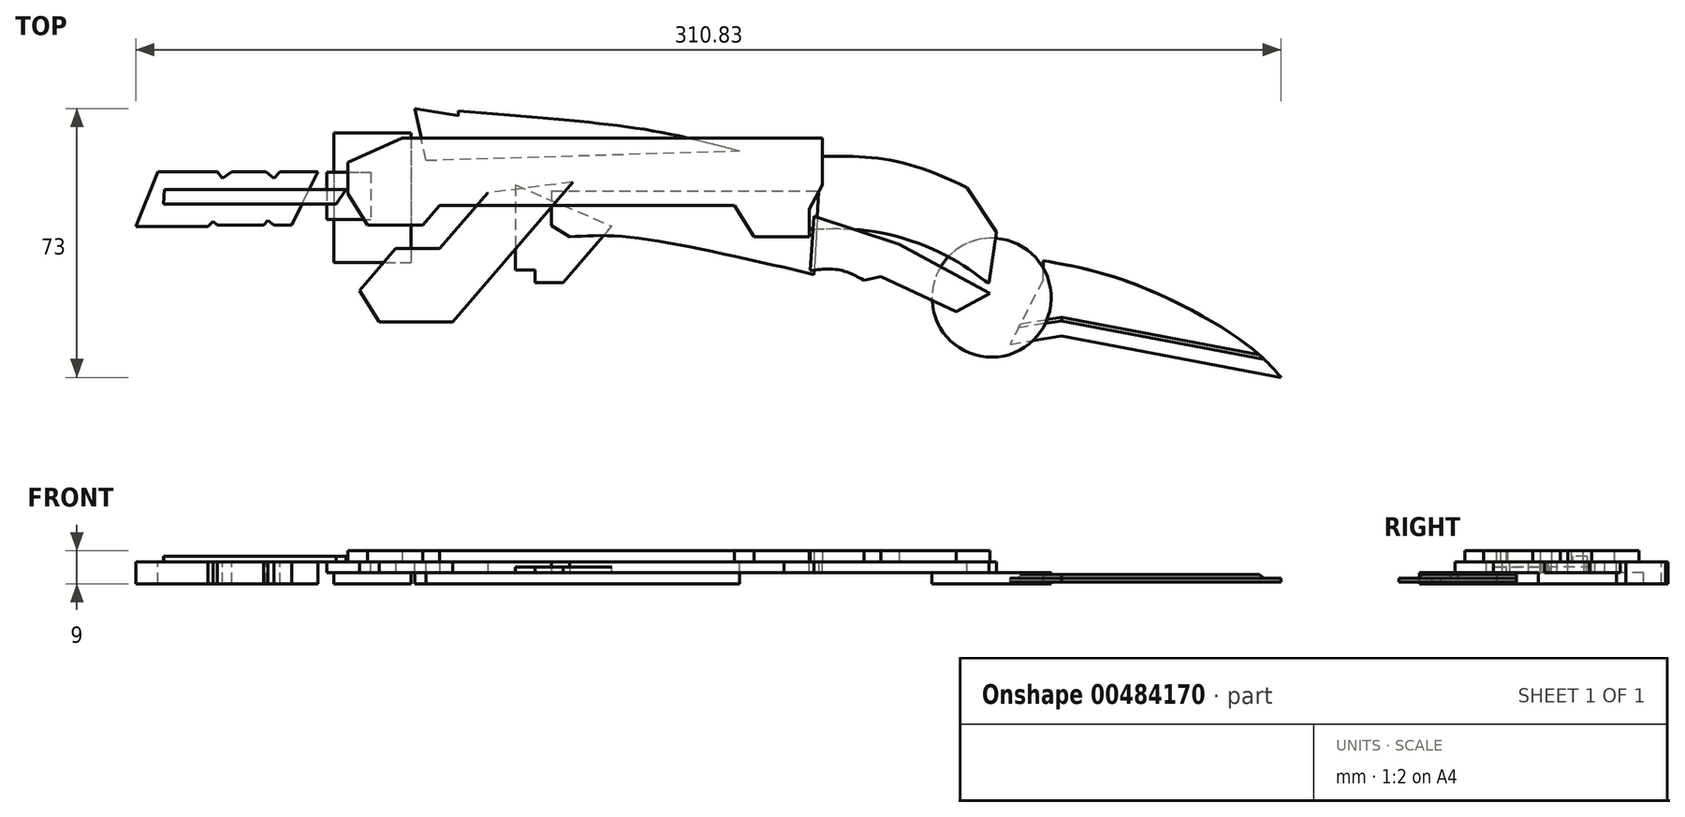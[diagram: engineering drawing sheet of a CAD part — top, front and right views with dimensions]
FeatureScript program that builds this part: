
annotation { "Feature Type Name" : "Feature", "Feature Type Description" : "" }
export const myFeature = defineFeature(function(context is Context, id is Id, definition is map)
    precondition{}
    {
        {
            var Q0;
            Q0=qCreatedBy(makeId("Top.planeOp"),FACE);
            var sketch = newSketch(context, id + "F0", { "sketchPlane" : qUnion([Q0])});
            skLineSegment(sketch, "E0", {"start": v(-55.32, 8.46) * mm, "end": v(-50, 0) * mm});
            skLineSegment(sketch, "E1", {"start": v(-50, 0) * mm, "end": v(-30, 0) * mm});
            skLineSegment(sketch, "E2", {"start": v(-30, 0) * mm, "end": v(2.6, 37.91) * mm});
            skLineSegment(sketch, "E3", {"start": v(-55.32, 8.46) * mm, "end": v(-45.54, 19.83) * mm});
            skLineSegment(sketch, "E4", {"start": v(-45.54, 19.83) * mm, "end": v(-33.54, 19.83) * mm});
            skLineSegment(sketch, "E5", {"start": v(-33.54, 19.83) * mm, "end": v(-20.5, 35) * mm});
            skLineSegment(sketch, "E6", {"start": v(2.6, 37.91) * mm, "end": v(-20.5, 35) * mm});
            skSolve(sketch);
        }
        {
            var Q0;
            Q0=makeQuery(id+"F0.imprint","IMPRINT",FACE,{"disambiguationData":[TD([[makeQuery(id+"F0.imprint","IMPRINT",EDGE,{"derivedFrom":sQuery(id+"F0.wireOp",EDGE,"E0")}),1.0]])]});
            extrude(context, id + "F1", {"entities" : qUnion([Q0]), "depth" : 3 * mm});
        }
        {
            var Q0;
            Q0=makeQuery(id+"F1.opExtrude","CAP_FACE",FACE,{"disambiguationData":[OSD([sQuery(id+"F0.wireOp",EDGE,"E0"),sQuery(id+"F0.wireOp",EDGE,"E1"),sQuery(id+"F0.wireOp",EDGE,"E2"),sQuery(id+"F0.wireOp",EDGE,"E3"),sQuery(id+"F0.wireOp",EDGE,"E4"),sQuery(id+"F0.wireOp",EDGE,"E5"),sQuery(id+"F0.wireOp",EDGE,"gxwEivb7-eXaO-3uHs-wTHl-g3tFR2Pt1wvS")])],"isStart":false});
            var sketch = newSketch(context, id + "F2", { "sketchPlane" : qUnion([Q0])});
            skLineSegment(sketch, "E7", {"start": v(-58.44, 34.7) * mm, "end": v(-53.1, 26.23) * mm});
            skLineSegment(sketch, "E8", {"start": v(-53.1, 26.23) * mm, "end": v(-38.1, 26.23) * mm});
            skLineSegment(sketch, "E9", {"start": v(-38.1, 26.23) * mm, "end": v(-33.54, 31.54) * mm});
            skLineSegment(sketch, "E10", {"start": v(-33.54, 31.54) * mm, "end": v(46.46, 31.54) * mm});
            skLineSegment(sketch, "E11", {"start": v(46.46, 31.54) * mm, "end": v(51.8, 23.08) * mm});
            skLineSegment(sketch, "E12", {"start": v(51.8, 23.08) * mm, "end": v(66.8, 23.08) * mm});
            skLineSegment(sketch, "E13", {"start": v(66.8, 23.08) * mm, "end": v(66.8, 30.58) * mm});
            skLineSegment(sketch, "E14", {"start": v(66.8, 30.58) * mm, "end": v(70.28, 37.11) * mm});
            skLineSegment(sketch, "E15", {"start": v(70.28, 37.11) * mm, "end": v(70.28, 49.91) * mm});
            skLineSegment(sketch, "E16", {"start": v(-58.44, 34.7) * mm, "end": v(-58.44, 43.2) * mm});
            skLineSegment(sketch, "E17", {"start": v(70.28, 49.91) * mm, "end": v(-43.72, 49.91) * mm});
            skLineSegment(sketch, "E18", {"start": v(-43.72, 49.91) * mm, "end": v(-58.44, 43.2) * mm});
            skSolve(sketch);
        }
        {
            var Q0;
            Q0=makeQuery(id+"F1.opExtrude","CAP_FACE",FACE,{"disambiguationData":[OSD([sQuery(id+"F0.wireOp",EDGE,"E0"),sQuery(id+"F0.wireOp",EDGE,"E1"),sQuery(id+"F0.wireOp",EDGE,"E2"),sQuery(id+"F0.wireOp",EDGE,"E3"),sQuery(id+"F0.wireOp",EDGE,"E4"),sQuery(id+"F0.wireOp",EDGE,"E5"),sQuery(id+"F0.wireOp",EDGE,"E6")])],"isStart":false});
            var sketch = newSketch(context, id + "F3", { "sketchPlane" : qUnion([Q0])});
            skLineSegment(sketch, "E19", {"start": v(-20.5, 35) * mm, "end": v(2.6, 37.91) * mm});
            skLineSegment(sketch, "E20", {"start": v(2.6, 37.91) * mm, "end": v(-2.86, 31.55) * mm});
            skLineSegment(sketch, "E21", {"start": v(-2.86, 31.55) * mm, "end": v(-23.48, 31.54) * mm});
            skLineSegment(sketch, "E22", {"start": v(-23.48, 31.54) * mm, "end": v(-20.5, 35) * mm});
            skSolve(sketch);
        }
        {
            var Q0;
            Q0 = qSketchRegion(id + "F3", true);
            extrude(context, id + "F4", {"entities" : qUnion([Q0]), "depth" : 3 * mm});
        }
        {
            var Q0;
            Q0 = qSketchRegion(id + "F2", true);
            extrude(context, id + "F5", {"entities" : qUnion([Q0]), "depth" : 3 * mm});
        }
        {
            var Q0;
            Q0=makeQuery(id+"F4.opExtrude","SWEPT_BODY",BODY,{"disambiguationData":[OSD([sQuery(id+"F3.wireOp",EDGE,"E19"),sQuery(id+"F3.wireOp",EDGE,"E20"),sQuery(id+"F3.wireOp",EDGE,"E21"),sQuery(id+"F3.wireOp",EDGE,"E22")])]});
            var Q1;
            Q1=makeQuery(id+"F5.opExtrude","SWEPT_BODY",BODY,{"disambiguationData":[OSD([sQuery(id+"F2.wireOp",EDGE,"E7"),sQuery(id+"F2.wireOp",EDGE,"E8"),sQuery(id+"F2.wireOp",EDGE,"E9"),sQuery(id+"F2.wireOp",EDGE,"E10"),sQuery(id+"F2.wireOp",EDGE,"E11"),sQuery(id+"F2.wireOp",EDGE,"E12"),sQuery(id+"F2.wireOp",EDGE,"E13"),sQuery(id+"F2.wireOp",EDGE,"E14"),sQuery(id+"F2.wireOp",EDGE,"E15"),sQuery(id+"F2.wireOp",EDGE,"E16"),sQuery(id+"F2.wireOp",EDGE,"E17"),sQuery(id+"F2.wireOp",EDGE,"E18")])]});
            booleanBodies(context, id + "F6", {"operationType" : BooleanOperationType.UNION, "tools" : qUnion([Q0, Q1])});
        }
        {
            var Q0;
            Q0=makeQuery(id+"F6.opBoolean","MERGE",FACE,{"derivedFrom":[makeQuery(id+"F4.opExtrude","CAP_FACE",FACE,{"disambiguationData":[OSD([sQuery(id+"F3.wireOp",EDGE,"E19"),sQuery(id+"F3.wireOp",EDGE,"E20"),sQuery(id+"F3.wireOp",EDGE,"E21"),sQuery(id+"F3.wireOp",EDGE,"E22")])],"isStart":true}),makeQuery(id+"F5.opExtrude","CAP_FACE",FACE,{"disambiguationData":[OSD([sQuery(id+"F2.wireOp",EDGE,"E7"),sQuery(id+"F2.wireOp",EDGE,"E8"),sQuery(id+"F2.wireOp",EDGE,"E9"),sQuery(id+"F2.wireOp",EDGE,"E10"),sQuery(id+"F2.wireOp",EDGE,"E11"),sQuery(id+"F2.wireOp",EDGE,"E12"),sQuery(id+"F2.wireOp",EDGE,"E13"),sQuery(id+"F2.wireOp",EDGE,"E14"),sQuery(id+"F2.wireOp",EDGE,"E15"),sQuery(id+"F2.wireOp",EDGE,"E16"),sQuery(id+"F2.wireOp",EDGE,"E17"),sQuery(id+"F2.wireOp",EDGE,"E18")])],"isStart":true})]});
            var sketch = newSketch(context, id + "F7", { "sketchPlane" : qUnion([Q0])});
            skFitSpline(sketch, "E23", {"points": [v(67.93, -44.79) * mm, v(91.44, -43.3) * mm, v(118.68, -31.91) * mm], "startDerivative": vector(49.42, -1.17) * mm, "endDerivative": vector(52.04, 26.4) * mm});
            skFitSpline(sketch, "E24", {"points": [v(62.89, -24.82) * mm, v(84.72, -24.45) * mm, v(107.67, -15.86) * mm, v(115.51, -10.45) * mm, v(115.89, -10.45) * mm], "startDerivative": vector(60.83, -3.9) * mm, "endDerivative": vector(6.34, -2.01) * mm});
            skLineSegment(sketch, "E25", {"start": v(67.93, -44.79) * mm, "end": v(62.89, -24.82) * mm});
            skLineSegment(sketch, "E26", {"start": v(117.56, -24.27) * mm, "end": v(115.51, -10.45) * mm});
            skLineSegment(sketch, "E27", {"start": v(109.52, -36.56) * mm, "end": v(117.56, -24.27) * mm});
            skSolve(sketch);
        }
        {
            var Q0;
            {var subQ0=sQuery(id+"F7.wireOp",EDGE,"E26");Q0=makeQuery(id+"F7.imprint","IMPRINT",FACE,{"disambiguationData":[TD([[makeQuery(id+"F7.imprint","IMPRINT",EDGE,{"derivedFrom":subQ0}),1.0]])]});}
            extrude(context, id + "F8", {"entities" : qUnion([Q0]), "depth" : 3 * mm});
        }
        {
            var Q0;
            Q0=makeQuery(id+"F8.opExtrude","CAP_FACE",FACE,{"disambiguationData":[OSD([sQuery(id+"F2.wireOp",EDGE,"E13"),sQuery(id+"F2.wireOp",EDGE,"E14"),sQuery(id+"F2.wireOp",EDGE,"E15"),sQuery(id+"F7.wireOp",EDGE,"E23"),sQuery(id+"F7.wireOp",EDGE,"E24"),sQuery(id+"F7.wireOp",EDGE,"E26"),sQuery(id+"F7.wireOp",EDGE,"E27")])],"isStart":false});
            var sketch = newSketch(context, id + "F9", { "sketchPlane" : qUnion([Q0])});
            skCircle(sketch, "E28", {"center": v(116.26, -6.53) * mm, "radius": 16.16 * mm});
            skSolve(sketch);
        }
        {
            var Q0;
            Q0 = qSketchRegion(id + "F9", true);
            extrude(context, id + "F10", {"entities" : qUnion([Q0]), "depth" : 3 * mm});
        }
        {
            var Q0;
            Q0=qCreatedBy(makeId("Top.planeOp"),FACE);
            cPlane(context, id + "F11", {"entities" : qUnion([Q0]), "cplaneType" : CPlaneType.OFFSET, "offset" : 1.5 * mm, "oppositeDirection" : true, "width" : 150 * mm, "height" : 150 * mm});
        }
        {
            var Q0;
            Q0=qCreatedBy(id+"F11.planeOp",FACE);
            var sketch = newSketch(context, id + "F12", { "sketchPlane" : qUnion([Q0])});
            skLineSegment(sketch, "E29", {"start": v(130.23, 11.38) * mm, "end": v(130.23, 16.6) * mm});
            skFitSpline(sketch, "E30", {"points": [v(130.23, 16.6) * mm, v(153.93, 10.64) * mm, v(184.83, -5.65) * mm, v(194.86, -15.15) * mm], "startDerivative": vector(65.46, -11.77) * mm, "endDerivative": vector(31.18, -35.34) * mm});
            skLineSegment(sketch, "E31", {"start": v(121.23, -6.18) * mm, "end": v(135.22, -3.8) * mm});
            skLineSegment(sketch, "E32", {"start": v(135.22, -3.8) * mm, "end": v(194.86, -15.15) * mm});
            skLineSegment(sketch, "E33", {"start": v(130.23, 11.38) * mm, "end": v(121.23, -6.18) * mm});
            skSolve(sketch);
        }
        {
            var Q0;
            Q0=makeQuery(id+"F12.imprint","IMPRINT",FACE,{"disambiguationData":[TD([[makeQuery(id+"F12.imprint","IMPRINT",EDGE,{"derivedFrom":sQuery(id+"F12.wireOp",EDGE,"E29")}),-1.0]])]});
            extrude(context, id + "F13", {"entities" : qUnion([Q0]), "depth" : 1 * mm});
        }
        {
            var Q0;
            Q0=makeQuery(id+"F13.opExtrude","CAP_FACE",FACE,{"disambiguationData":[OSD([sQuery(id+"F12.wireOp",EDGE,"E29"),sQuery(id+"F12.wireOp",EDGE,"E30"),sQuery(id+"F12.wireOp",EDGE,"E31"),sQuery(id+"F12.wireOp",EDGE,"E32"),sQuery(id+"F12.wireOp",EDGE,"E33")])],"isStart":true});
            extrude(context, id + "F14", {"entities" : qUnion([Q0]), "depth" : 1 * mm});
        }
        {
            var Q0;
            Q0=makeQuery(id+"F13.opExtrude","CAP_EDGE",EDGE,{"disambiguationData":[OSD([sQuery(id+"F12.wireOp",EDGE,"E31")])],"isStart":false});
            var Q1;
            Q1=makeQuery(id+"F13.opExtrude","CAP_EDGE",EDGE,{"disambiguationData":[OSD([sQuery(id+"F12.wireOp",EDGE,"E32")])],"isStart":false});
            chamfer(context, id + "F15", {"entities" : qUnion([Q0, Q1]), "width" : 5 * mm, "tangentPropagation" : true});
        }
        {
            var Q0;
            Q0=qCreatedBy(makeId("Top.planeOp"),FACE);
            var sketch = newSketch(context, id + "F16", { "sketchPlane" : qUnion([Q0])});
            skLineSegment(sketch, "E34", {"start": v(-13.01, 37.14) * mm, "end": v(-13.01, 14) * mm});
            skLineSegment(sketch, "E35", {"start": v(-13.01, 14) * mm, "end": v(-7.6, 14) * mm});
            skLineSegment(sketch, "E36", {"start": v(-7.6, 14) * mm, "end": v(-7.6, 10.64) * mm});
            skLineSegment(sketch, "E37", {"start": v(-7.6, 10.64) * mm, "end": v(0, 10.64) * mm});
            skLineSegment(sketch, "E38", {"start": v(0, 10.64) * mm, "end": v(13.16, 25.94) * mm});
            skLineSegment(sketch, "E39", {"start": v(-13.01, 37.14) * mm, "end": v(13.16, 25.94) * mm});
            skSolve(sketch);
        }
        {
            var Q0;
            Q0=makeQuery(id+"F16.imprint","IMPRINT",FACE,{"disambiguationData":[TD([[makeQuery(id+"F16.imprint","IMPRINT",EDGE,{"derivedFrom":sQuery(id+"F16.wireOp",EDGE,"E34")}),1.0]])]});
            extrude(context, id + "F17", {"entities" : qUnion([Q0]), "oppositeDirection" : true, "depth" : 1.5 * mm});
        }
        {
            var Q0;
            Q0=makeQuery(id+"F17.opExtrude","CAP_FACE",FACE,{"disambiguationData":[OSD([sQuery(id+"F16.wireOp",EDGE,"E34"),sQuery(id+"F16.wireOp",EDGE,"E35"),sQuery(id+"F16.wireOp",EDGE,"E36"),sQuery(id+"F16.wireOp",EDGE,"E37"),sQuery(id+"F16.wireOp",EDGE,"E38"),sQuery(id+"F16.wireOp",EDGE,"E39")])],"isStart":true});
            var sketch = newSketch(context, id + "F18", { "sketchPlane" : qUnion([Q0])});
            skLineSegment(sketch, "E40", {"start": v(-3.16, 35.53) * mm, "end": v(-3.16, 26.1) * mm});
            skLineSegment(sketch, "E41", {"start": v(-3.16, 26.1) * mm, "end": v(1.75, 23.02) * mm});
            skFitSpline(sketch, "E42", {"points": [v(1.75, 23.02) * mm, v(17.22, 23.02) * mm, v(59.95, 14.74) * mm], "startDerivative": vector(36.41, 2.47) * mm, "endDerivative": vector(76.6, -17.35) * mm});
            skLineSegment(sketch, "E43", {"start": v(-3.16, 35.53) * mm, "end": v(59.2, 35.53) * mm});
            skFitSpline(sketch, "E44", {"points": [v(59.95, 14.74) * mm, v(68.07, 12.79) * mm], "startDerivative": vector(8.12, -1.96) * mm, "endDerivative": vector(8.12, -1.96) * mm});
            skLineSegment(sketch, "E45", {"start": v(59.2, 35.53) * mm, "end": v(69.33, 35.53) * mm});
            skLineSegment(sketch, "E46", {"start": v(69.33, 35.53) * mm, "end": v(68.07, 12.79) * mm});
            skSolve(sketch);
        }
        {
            var Q0;
            Q0 = qSketchRegion(id + "F18", true);
            extrude(context, id + "F19", {"entities" : qUnion([Q0]), "depth" : 3 * mm});
        }
        {
            var Q0;
            Q0=makeQuery(id+"F19.opExtrude","CAP_FACE",FACE,{"disambiguationData":[OSD([sQuery(id+"F18.wireOp",EDGE,"E40"),sQuery(id+"F18.wireOp",EDGE,"E41"),sQuery(id+"F18.wireOp",EDGE,"E42"),sQuery(id+"F18.wireOp",EDGE,"E43"),sQuery(id+"F18.wireOp",EDGE,"E44"),sQuery(id+"F18.wireOp",EDGE,"E45"),sQuery(id+"F18.wireOp",EDGE,"E46")])],"isStart":false});
            var sketch = newSketch(context, id + "F20", { "sketchPlane" : qUnion([Q0])});
            skFitSpline(sketch, "E47", {"points": [v(67.05, 13.88) * mm, v(74.98, 14.07) * mm, v(81.6, 11.27) * mm], "startDerivative": vector(15.97, 1.93) * mm, "endDerivative": vector(13.12, -7.23) * mm});
            skLineSegment(sketch, "E48", {"start": v(81.6, 11.27) * mm, "end": v(86.27, 12.3) * mm});
            skLineSegment(sketch, "E49", {"start": v(86.27, 12.3) * mm, "end": v(106.7, 2.68) * mm});
            skLineSegment(sketch, "E50", {"start": v(106.7, 2.68) * mm, "end": v(115.85, 7.72) * mm});
            skLineSegment(sketch, "E51", {"start": v(115.85, 7.72) * mm, "end": v(91.21, 21.06) * mm});
            skLineSegment(sketch, "E52", {"start": v(91.21, 21.06) * mm, "end": v(68.07, 28.62) * mm});
            skLineSegment(sketch, "E53", {"start": v(68.07, 28.62) * mm, "end": v(67.05, 13.88) * mm});
            skSolve(sketch);
        }
        {
            var Q0;
            {var subQ0=sQuery(id+"F20.wireOp",EDGE,"E53");Q0=makeQuery(id+"F20.imprint","IMPRINT",FACE,{"disambiguationData":[TD([[makeQuery(id+"F20.imprint","IMPRINT",EDGE,{"derivedFrom":subQ0}),1.0]])]});}
            var Q1;
            {var subQ0=sQuery(id+"F20.wireOp",EDGE,"E48");Q1=makeQuery(id+"F20.imprint","IMPRINT",FACE,{"disambiguationData":[TD([[makeQuery(id+"F20.imprint","IMPRINT",EDGE,{"derivedFrom":subQ0}),1.0]])]});}
            extrude(context, id + "F21", {"entities" : qUnion([Q0, Q1]), "depth" : 3 * mm});
        }
        {
            var Q0;
            Q0=makeQuery(id+"F6.opBoolean","MERGE",FACE,{"derivedFrom":[makeQuery(id+"F4.opExtrude","CAP_FACE",FACE,{"disambiguationData":[OSD([sQuery(id+"F3.wireOp",EDGE,"E19"),sQuery(id+"F3.wireOp",EDGE,"E20"),sQuery(id+"F3.wireOp",EDGE,"E21"),sQuery(id+"F3.wireOp",EDGE,"E22")])],"isStart":true}),makeQuery(id+"F5.opExtrude","CAP_FACE",FACE,{"disambiguationData":[OSD([sQuery(id+"F2.wireOp",EDGE,"E7"),sQuery(id+"F2.wireOp",EDGE,"E8"),sQuery(id+"F2.wireOp",EDGE,"E9"),sQuery(id+"F2.wireOp",EDGE,"E10"),sQuery(id+"F2.wireOp",EDGE,"E11"),sQuery(id+"F2.wireOp",EDGE,"E12"),sQuery(id+"F2.wireOp",EDGE,"E13"),sQuery(id+"F2.wireOp",EDGE,"E14"),sQuery(id+"F2.wireOp",EDGE,"E15"),sQuery(id+"F2.wireOp",EDGE,"E16"),sQuery(id+"F2.wireOp",EDGE,"E17"),sQuery(id+"F2.wireOp",EDGE,"E18")])],"isStart":true})]});
            var sketch = newSketch(context, id + "F22", { "sketchPlane" : qUnion([Q0])});
            skLineSegment(sketch, "E54", {"start": v(-37.27, -43.85) * mm, "end": v(-40.26, -57.85) * mm});
            skLineSegment(sketch, "E55", {"start": v(-40.26, -57.85) * mm, "end": v(-28.5, -55.98) * mm});
            skLineSegment(sketch, "E56", {"start": v(-28.5, -55.98) * mm, "end": v(-28.5, -57.16) * mm});
            skFitSpline(sketch, "E57", {"points": [v(-28.5, -57.16) * mm, v(4.36, -54.39) * mm, v(27.29, -51.3) * mm, v(47.87, -46.41) * mm], "startDerivative": vector(90.56, 7.09) * mm, "endDerivative": vector(67.52, 17.59) * mm});
            skLineSegment(sketch, "E58", {"start": v(-37.27, -43.85) * mm, "end": v(47.87, -46.41) * mm});
            skSolve(sketch);
        }
        {
            var Q0;
            {var subQ4=sQuery(id+"F22.wireOp",EDGE,"E55");Q0=makeQuery(id+"F22.imprint","IMPRINT",FACE,{"disambiguationData":[TD([[makeQuery(id+"F22.imprint","IMPRINT",EDGE,{"derivedFrom":subQ4}),1.0]])]});}
            var Q1;
            {var subQ0=sQuery(id+"F22.wireOp",EDGE,"E58");Q1=makeQuery(id+"F22.imprint","IMPRINT",FACE,{"disambiguationData":[TD([[makeQuery(id+"F22.imprint","IMPRINT",EDGE,{"derivedFrom":subQ0}),-1.0]])]});}
            extrude(context, id + "F23", {"entities" : qUnion([Q0, Q1]), "depth" : 6 * mm});
        }
        {
            var Q0;
            Q0=makeQuery(id+"F6.opBoolean","MERGE",FACE,{"derivedFrom":[makeQuery(id+"F4.opExtrude","CAP_FACE",FACE,{"disambiguationData":[OSD([sQuery(id+"F3.wireOp",EDGE,"E19"),sQuery(id+"F3.wireOp",EDGE,"E20"),sQuery(id+"F3.wireOp",EDGE,"E21"),sQuery(id+"F3.wireOp",EDGE,"E22")])],"isStart":true}),makeQuery(id+"F5.opExtrude","CAP_FACE",FACE,{"disambiguationData":[OSD([sQuery(id+"F2.wireOp",EDGE,"E7"),sQuery(id+"F2.wireOp",EDGE,"E8"),sQuery(id+"F2.wireOp",EDGE,"E9"),sQuery(id+"F2.wireOp",EDGE,"E10"),sQuery(id+"F2.wireOp",EDGE,"E11"),sQuery(id+"F2.wireOp",EDGE,"E12"),sQuery(id+"F2.wireOp",EDGE,"E13"),sQuery(id+"F2.wireOp",EDGE,"E14"),sQuery(id+"F2.wireOp",EDGE,"E15"),sQuery(id+"F2.wireOp",EDGE,"E16"),sQuery(id+"F2.wireOp",EDGE,"E17"),sQuery(id+"F2.wireOp",EDGE,"E18")])],"isStart":true})]});
            var sketch = newSketch(context, id + "F24", { "sketchPlane" : qUnion([Q0])});
            skLineSegment(sketch, "E59.bottom", {"start": v(-64.17, -40.62) * mm, "end": v(-52.24, -40.62) * mm});
            skLineSegment(sketch, "E59.top", {"start": v(-64.17, -27.75) * mm, "end": v(-52.24, -27.75) * mm});
            skLineSegment(sketch, "E59.left", {"start": v(-64.17, -40.62) * mm, "end": v(-64.17, -27.75) * mm});
            skLineSegment(sketch, "E59.right", {"start": v(-52.24, -40.62) * mm, "end": v(-52.24, -27.75) * mm});
            skSolve(sketch);
        }
        {
            var Q0;
            {var subQ5=sQuery(id+"F24.wireOp",EDGE,"E59.left");Q0=makeQuery(id+"F24.imprint","IMPRINT",FACE,{"disambiguationData":[TD([[makeQuery(id+"F24.imprint","IMPRINT",EDGE,{"derivedFrom":subQ5}),-1.0]])]});}
            var Q1;
            {var subQ5=sQuery(id+"F24.wireOp",EDGE,"E59.right");Q1=makeQuery(id+"F24.imprint","IMPRINT",FACE,{"disambiguationData":[TD([[makeQuery(id+"F24.imprint","IMPRINT",EDGE,{"derivedFrom":subQ5}),1.0]])]});}
            extrude(context, id + "F25", {"entities" : qUnion([Q0, Q1]), "depth" : 3 * mm});
        }
        {
            var Q0;
            Q0=makeQuery(id+"F25.opExtrude","CAP_FACE",FACE,{"disambiguationData":[OSD([sQuery(id+"F24.wireOp",EDGE,"E59.bottom"),sQuery(id+"F24.wireOp",EDGE,"E59.top"),sQuery(id+"F24.wireOp",EDGE,"E59.left"),sQuery(id+"F24.wireOp",EDGE,"E59.right")])],"isStart":false});
            var sketch = newSketch(context, id + "F26", { "sketchPlane" : qUnion([Q0])});
            skLineSegment(sketch, "E60.bottom", {"start": v(-62.31, -51.2) * mm, "end": v(-41.28, -51.2) * mm});
            skLineSegment(sketch, "E60.top", {"start": v(-62.31, -16.06) * mm, "end": v(-41.28, -16.06) * mm});
            skLineSegment(sketch, "E60.left", {"start": v(-62.31, -51.2) * mm, "end": v(-62.31, -16.06) * mm});
            skLineSegment(sketch, "E60.right", {"start": v(-41.28, -51.2) * mm, "end": v(-41.28, -16.06) * mm});
            skSolve(sketch);
        }
        {
            var Q0;
            Q0 = qSketchRegion(id + "F26", true);
            extrude(context, id + "F27", {"entities" : qUnion([Q0]), "depth" : 3 * mm});
        }
        {
            var Q0;
            Q0=makeQuery(id+"F25.opExtrude","CAP_FACE",FACE,{"disambiguationData":[OSD([sQuery(id+"F24.wireOp",EDGE,"E59.bottom"),sQuery(id+"F24.wireOp",EDGE,"E59.top"),sQuery(id+"F24.wireOp",EDGE,"E59.left"),sQuery(id+"F24.wireOp",EDGE,"E59.right")])],"isStart":true});
            var sketch = newSketch(context, id + "F28", { "sketchPlane" : qUnion([Q0])});
            skLineSegment(sketch, "E61", {"start": v(-59, 35.85) * mm, "end": v(-61.63, 31.96) * mm});
            skLineSegment(sketch, "E62", {"start": v(-61.63, 31.96) * mm, "end": v(-108.44, 31.96) * mm});
            skLineSegment(sketch, "E63", {"start": v(-59, 35.85) * mm, "end": v(-108.25, 35.85) * mm});
            skLineSegment(sketch, "E64", {"start": v(-108.25, 35.85) * mm, "end": v(-108.44, 31.96) * mm});
            skSolve(sketch);
        }
        {
            var Q0;
            Q0 = qSketchRegion(id + "F28", true);
            extrude(context, id + "F29", {"entities" : qUnion([Q0]), "depth" : 1.5 * mm});
        }
        {
            var Q0;
            Q0=makeQuery(id+"F29.opExtrude","CAP_FACE",FACE,{"disambiguationData":[OSD([sQuery(id+"F28.wireOp",EDGE,"E61"),sQuery(id+"F28.wireOp",EDGE,"E62"),sQuery(id+"F28.wireOp",EDGE,"E63"),sQuery(id+"F28.wireOp",EDGE,"E64")])],"isStart":true});
            var sketch = newSketch(context, id + "F30", { "sketchPlane" : qUnion([Q0])});
            skLineSegment(sketch, "E65", {"start": v(-66.56, -40.77) * mm, "end": v(-76.86, -40.77) * mm});
            skLineSegment(sketch, "E66", {"start": v(-76.86, -40.77) * mm, "end": v(-78.5, -38.9) * mm});
            skLineSegment(sketch, "E67", {"start": v(-78.5, -38.9) * mm, "end": v(-80.62, -40.77) * mm});
            skLineSegment(sketch, "E68", {"start": v(-80.62, -40.77) * mm, "end": v(-89.98, -40.77) * mm});
            skLineSegment(sketch, "E69", {"start": v(-89.98, -40.77) * mm, "end": v(-92.48, -38.9) * mm});
            skLineSegment(sketch, "E70", {"start": v(-92.48, -38.9) * mm, "end": v(-93.88, -40.77) * mm});
            skLineSegment(sketch, "E71", {"start": v(-93.88, -40.77) * mm, "end": v(-110.03, -40.77) * mm});
            skLineSegment(sketch, "E72", {"start": v(-110.03, -40.77) * mm, "end": v(-115.97, -25.84) * mm});
            skLineSegment(sketch, "E73", {"start": v(-115.97, -25.84) * mm, "end": v(-96.44, -25.84) * mm});
            skLineSegment(sketch, "E74", {"start": v(-96.44, -25.84) * mm, "end": v(-94.99, -27.3) * mm});
            skLineSegment(sketch, "E75", {"start": v(-94.99, -27.3) * mm, "end": v(-93.88, -26.18) * mm});
            skLineSegment(sketch, "E76", {"start": v(-93.88, -26.18) * mm, "end": v(-81.27, -26.18) * mm});
            skLineSegment(sketch, "E77", {"start": v(-81.27, -26.18) * mm, "end": v(-80.21, -27.56) * mm});
            skLineSegment(sketch, "E78", {"start": v(-80.21, -27.56) * mm, "end": v(-78.5, -26.24) * mm});
            skLineSegment(sketch, "E79", {"start": v(-78.5, -26.24) * mm, "end": v(-73.75, -26.24) * mm});
            skLineSegment(sketch, "E80", {"start": v(-73.75, -26.24) * mm, "end": v(-66.56, -40.77) * mm});
            skSolve(sketch);
        }
        {
            var Q0;
            Q0 = qSketchRegion(id + "F30", true);
            extrude(context, id + "F31", {"entities" : qUnion([Q0]), "depth" : 6 * mm});
        }
        {
            var Q0;
            Q0=makeQuery(id+"F17.opExtrude","SWEPT_BODY",BODY,{"disambiguationData":[OSD([sQuery(id+"F16.wireOp",EDGE,"E34"),sQuery(id+"F16.wireOp",EDGE,"E35"),sQuery(id+"F16.wireOp",EDGE,"E36"),sQuery(id+"F16.wireOp",EDGE,"E37"),sQuery(id+"F16.wireOp",EDGE,"E38"),sQuery(id+"F16.wireOp",EDGE,"E39")])]});
            transform(context, id + "F32", {"entities" : qUnion([Q0]), "transformType" : TransformType.TRANSLATION_3D, "dx" : 0 * mm, "dy" : 0 * mm, "dz" : 1.5 * mm, "makeCopy" : false});
        }
    });
